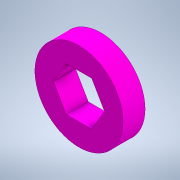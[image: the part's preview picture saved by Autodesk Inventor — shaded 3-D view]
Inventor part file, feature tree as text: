
AUTODESK INVENTOR PART (.ipt)
format: ipt  version: 2021.2 (Build 252289000, 289)  size: 106,496 bytes
history: native  units: in
note: dims shown in document units (in); Inventor stores cm internally (conversion verified against a paired STEP export)
features: extrude x1, sketch x1
ambient origin geometry x8: Origin, YZ Plane, XZ Plane, XY Plane, X Axis, Y Axis, Z Axis, Center Point
bodies: Solid1 (feature_tree)
feature tree (2):
  extrude  "Extrusion1"  Depth=0.25in
  sketch  "Sketch1"  dims[d0=0.5in d2=1.0in d3=0.2113in d4=0.25in d5=0.0in]
